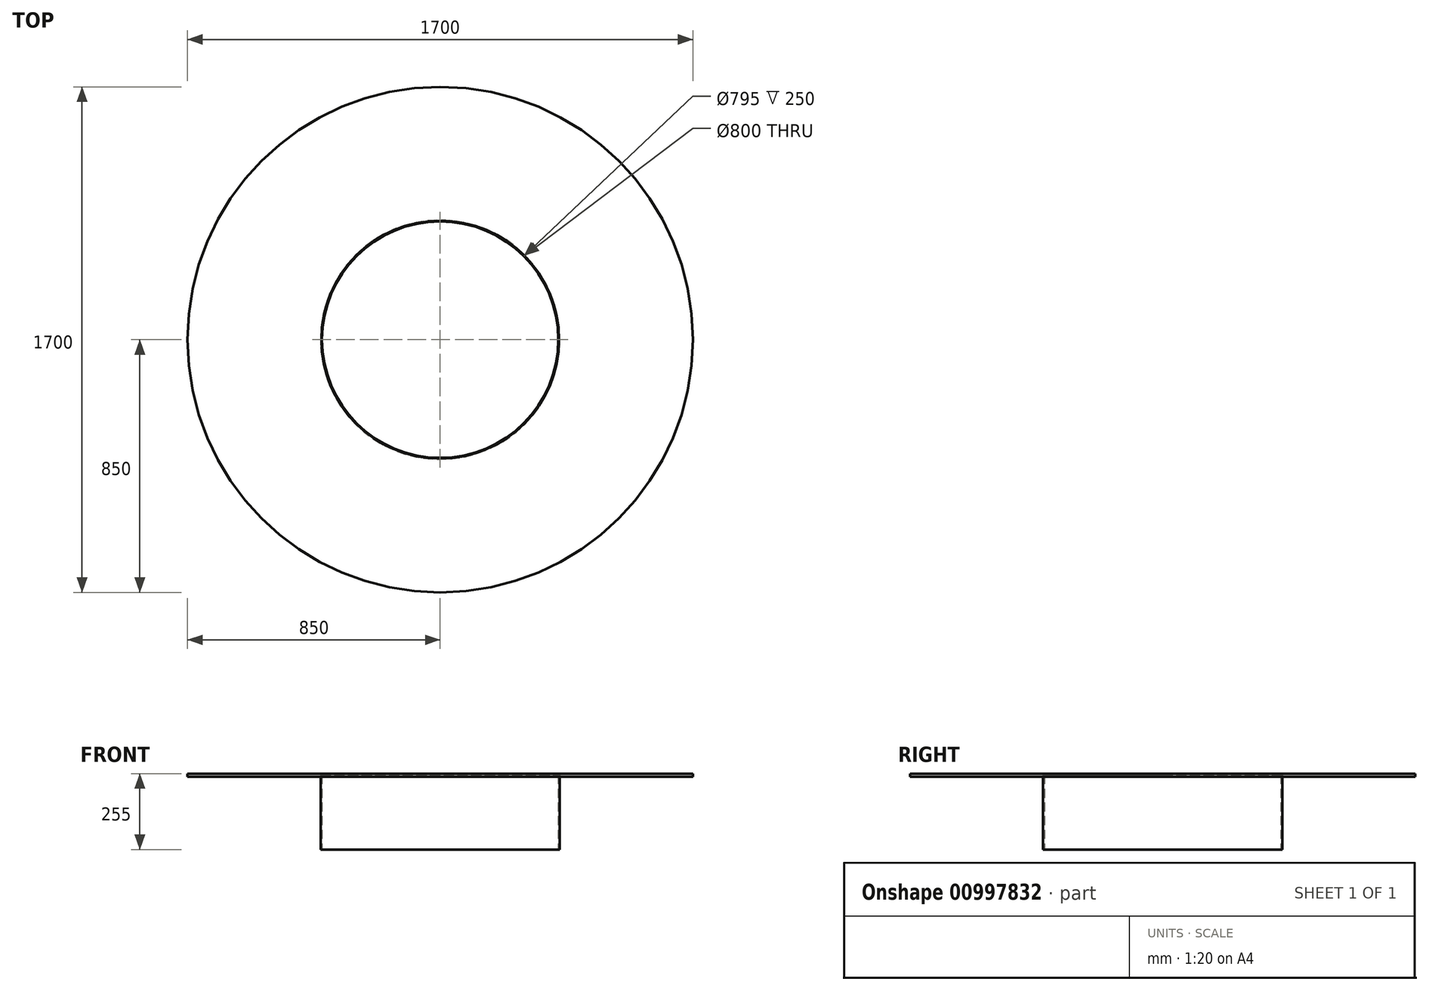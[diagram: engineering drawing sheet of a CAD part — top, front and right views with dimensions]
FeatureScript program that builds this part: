
annotation { "Feature Type Name" : "Feature", "Feature Type Description" : "" }
export const myFeature = defineFeature(function(context is Context, id is Id, definition is map)
    precondition{}
    {
        {
            var Q0;
            Q0=qCreatedBy(makeId("Front.planeOp"),FACE);
            var sketch = newSketch(context, id + "F0", { "sketchPlane" : qUnion([Q0])});
            skLineSegment(sketch, "E0", {"start": v(-1500, 0) * mm, "end": v(1500, 0) * mm, "construction": true});
            skLineSegment(sketch, "E1", {"start": v(-1500, 0) * mm, "end": v(-1561, 697.34) * mm});
            skLineSegment(sketch, "E2", {"start": v(0, 0) * mm, "end": v(0, 1400) * mm, "construction": true});
            skLineSegment(sketch, "E3", {"start": v(-400, 1420) * mm, "end": v(-850, 1420) * mm});
            skLineSegment(sketch, "E4", {"start": v(-850, 1420) * mm, "end": v(-850, 1400) * mm, "construction": true});
            skLineSegment(sketch, "E5", {"start": v(-850, 1400) * mm, "end": v(-400, 1400) * mm});
            skLineSegment(sketch, "E6", {"start": v(-400, 1400) * mm, "end": v(-400, 1420) * mm, "construction": true});
            skLineSegment(sketch, "E7", {"start": v(-860, 1410) * mm, "end": v(-1181.55, 1292.96) * mm});
            skArc(sketch, "E8", {"start": v(-1181.55, 1292.96) * mm, "mid": v(-1472.37, 1059.55) * mm, "end": v(-1561, 697.34) * mm});
            skCircle(sketch, "E9", {"center": v(-400, 1410) * mm, "radius": 10 * mm});
            skCircle(sketch, "E10", {"center": v(-850, 1410) * mm, "radius": 10 * mm});
            skCircle(sketch, "E11", {"center": v(-1500, 0) * mm, "radius": 10 * mm});
            skLineSegment(sketch, "E12", {"start": v(-400, 1410) * mm, "end": v(-400, 1160) * mm, "construction": true});
            skCircle(sketch, "E13", {"center": v(-400, 1160) * mm, "radius": 10 * mm});
            skLineSegment(sketch, "E14", {"start": v(-850, 1410) * mm, "end": v(-400, 1410) * mm, "construction": true});
            skPoint(sketch, "E15", {"position": v(-840, 1410) * mm});
            skPoint(sketch, "E16", {"position": v(-410, 1410) * mm});
            skPoint(sketch, "E17", {"position": v(-400, 1170) * mm});
            skLineSegment(sketch, "E18", {"start": v(-850, 1410) * mm, "end": v(-860, 1410) * mm, "construction": true});
            skPoint(sketch, "E19", {"position": v(-1500.87, 9.96) * mm});
            skSolve(sketch);
        }
        {
            var Q0;
            Q0=sQuery(id+"F0.wireOp",EDGE,"E11");
            var Q1;
            Q1=sQuery(id+"F0.wireOp",EDGE,"E10");
            var Q2;
            Q2=sQuery(id+"F0.wireOp",EDGE,"E9");
            var Q3;
            Q3=sQuery(id+"F0.wireOp",EDGE,"E13");
            var Q4;
            Q4=sQuery(id+"F0.wireOp",EDGE,"E2");
            revolve(context, id + "F1", {"bodyType" : ToolBodyType.SURFACE, "surfaceOperationType" : NewSurfaceOperationType.NEW, "surfaceEntities" : qUnion([Q0, Q1, Q2, Q3]), "axis" : qUnion([Q4]), "revolveType" : RevolveType.FULL});
        }
        {
            var Q0;
            Q0=sQuery(id+"F0.wireOp",EDGE,"E14");
            var Q1;
            Q1=qCreatedBy(makeId("Top.planeOp"),FACE);
            cPlane(context, id + "F2", {"entities" : qUnion([Q0, Q1]), "cplaneType" : CPlaneType.LINE_ANGLE, "offset" : 25 * mm, "angle" : 0 * degree, "width" : 150 * mm, "height" : 150 * mm});
        }
        {
            var Q0;
            Q0=sQuery(id+"F0.wireOp",VERTEX,"E16");
            var Q1;
            Q1=qCreatedBy(makeId("Right.planeOp"),FACE);
            cPlane(context, id + "F3", {"entities" : qUnion([Q0, Q1]), "cplaneType" : CPlaneType.PLANE_POINT, "offset" : 25 * mm, "width" : 150 * mm, "height" : 150 * mm});
        }
        {
            var Q0;
            Q0=qCreatedBy(id+"F3.planeOp",FACE);
            var sketch = newSketch(context, id + "F4", { "sketchPlane" : qUnion([Q0])});
            skCircle(sketch, "E20", {"center": v(0, 1410) * mm, "radius": 10 * mm});
            skSolve(sketch);
        }
        {
            var Q0;
            Q0 = qSketchRegion(id + "F4", true);
            var Q1;
            Q1=makeQuery(id+"F1.opRevolve","SWEPT_FACE",FACE,{"disambiguationData":[OSD([sQuery(id+"F0.wireOp",EDGE,"E10")])]});
            var Q2;
            Q2=sQuery(id+"F0.wireOp",VERTEX,"E15");
            extrude(context, id + "F5", {"entities" : qUnion([Q0]), "endBound" : BoundingType.UP_TO_VERTEX, "oppositeDirection" : true, "depth" : 25 * mm, "endBoundEntityFace" : qUnion([Q1]), "endBoundEntityVertex" : qUnion([Q2]), "offsetDistance" : 25 * mm});
        }
        {
            var Q0;
            Q0=sQuery(id+"F0.wireOp",VERTEX,"E17");
            var Q1;
            Q1=qCreatedBy(makeId("Top.planeOp"),FACE);
            cPlane(context, id + "F6", {"entities" : qUnion([Q0, Q1]), "cplaneType" : CPlaneType.PLANE_POINT, "offset" : 25 * mm, "width" : 150 * mm, "height" : 150 * mm});
        }
        {
            var Q0;
            Q0=qCreatedBy(id+"F6.planeOp",FACE);
            var sketch = newSketch(context, id + "F7", { "sketchPlane" : qUnion([Q0])});
            skCircle(sketch, "E21", {"center": v(-400, 0) * mm, "radius": 10 * mm});
            skSolve(sketch);
        }
        {
            var Q0;
            Q0 = qSketchRegion(id + "F7", true);
            var Q1;
            Q1=sQuery(id+"F0.wireOp",VERTEX,"E5.end");
            extrude(context, id + "F8", {"entities" : qUnion([Q0]), "endBound" : BoundingType.UP_TO_VERTEX, "depth" : 25 * mm, "endBoundEntityVertex" : qUnion([Q1]), "offsetDistance" : 25 * mm});
        }
        {
            var Q0;
            Q0=makeQuery(id+"F8.opExtrude","SWEPT_BODY",BODY,{"disambiguationData":[OSD([sQuery(id+"F7.wireOp",EDGE,"E21")])]});
            var Q1;
            Q1=makeQuery(id+"F5.opExtrude","SWEPT_BODY",BODY,{"disambiguationData":[OSD([sQuery(id+"F4.wireOp",EDGE,"E20")])]});
            var Q2;
            Q2=sQuery(id+"F0.wireOp",EDGE,"E2");
            circularPattern(context, id + "F9", {"entities" : qUnion([Q0, Q1]), "axis" : qUnion([Q2]), "angle" : 360 * degree, "instanceCount" : 16, "equalSpace" : true});
        }
        {
            var Q0;
            Q0=qCreatedBy(makeId("Top.planeOp"),FACE);
            cPlane(context, id + "F10", {"entities" : qUnion([Q0]), "cplaneType" : CPlaneType.OFFSET, "offset" : 10 * mm, "width" : 150 * mm, "height" : 150 * mm});
        }
        {
            var Q0;
            Q0=qCreatedBy(id+"F10.planeOp",FACE);
            var sketch = newSketch(context, id + "F11", { "sketchPlane" : qUnion([Q0])});
            skCircle(sketch, "E22", {"center": v(-1500.87, 0) * mm, "radius": 10 * mm});
            skSolve(sketch);
        }
        {
            var Q0;
            Q0=makeQuery(id+"F11.imprint","IMPRINT",FACE,{"disambiguationData":[TD([[makeQuery(id+"F11.imprint","IMPRINT",EDGE,{"derivedFrom":sQuery(id+"F11.wireOp",EDGE,"E22")}),1.0]])]});
            var Q1;
            Q1=sQuery(id+"F0.wireOp",EDGE,"E1");
            var Q2;
            Q2=sQuery(id+"F0.wireOp",EDGE,"E8");
            var Q3;
            Q3=sQuery(id+"F0.wireOp",EDGE,"E7");
            sweep(context, id + "F12", {"profiles" : qUnion([Q0]), "path" : qUnion([Q1, Q2, Q3])});
        }
        {
            var Q0;
            Q0=makeQuery(id+"F12.opSweep","SWEPT_BODY",BODY,{"disambiguationData":[OSD([sQuery(id+"F0.wireOp",EDGE,"E7"),sQuery(id+"F11.wireOp",EDGE,"E22")])]});
            var Q1;
            Q1=sQuery(id+"F0.wireOp",EDGE,"E2");
            circularPattern(context, id + "F13", {"entities" : qUnion([Q0]), "axis" : qUnion([Q1]), "angle" : 360 * degree, "instanceCount" : 20, "equalSpace" : true});
        }
        {
            var Q0;
            Q0=qCreatedBy(makeId("Front.planeOp"),FACE);
            var sketch = newSketch(context, id + "F14", { "sketchPlane" : qUnion([Q0])});
            skLineSegment(sketch, "E23.bottom", {"start": v(-1630, 1509.63) * mm, "end": v(1696.87, 1509.63) * mm});
            skLineSegment(sketch, "E23.top", {"start": v(-1630, -136) * mm, "end": v(1696.87, -136) * mm});
            skLineSegment(sketch, "E23.left", {"start": v(-1630, 1509.63) * mm, "end": v(-1630, -136) * mm});
            skLineSegment(sketch, "E23.right", {"start": v(1696.87, 1509.63) * mm, "end": v(1696.87, -136) * mm});
            skSolve(sketch);
        }
        {
            var Q0;
            Q0 = qSketchRegion(id + "F14", true);
            extrude(context, id + "F15", {"entities" : qUnion([Q0]), "operationType" : NewBodyOperationType.REMOVE, "endBound" : BoundingType.SYMMETRIC, "oppositeDirection" : true, "depth" : 4000 * mm, "offsetDistance" : 25 * mm});
        }
        {
            var Q0;
            Q0=qCreatedBy(id+"F2.planeOp",FACE);
            var sketch = newSketch(context, id + "F16", { "sketchPlane" : qUnion([Q0])});
            skCircle(sketch, "E24", {"center": v(0, 0) * mm, "radius": 850 * mm});
            skCircle(sketch, "E25", {"center": v(0, 0) * mm, "radius": 400 * mm});
            skSolve(sketch);
        }
        {
            var Q0;
            Q0=makeQuery(id+"F16.imprint","IMPRINT",FACE,{"disambiguationData":[TD([[makeQuery(id+"F16.imprint","IMPRINT",EDGE,{"derivedFrom":sQuery(id+"F16.wireOp",EDGE,"E24")}),1.0]])]});
            extrude(context, id + "F17", {"entities" : qUnion([Q0]), "endBound" : BoundingType.SYMMETRIC, "depth" : 10 * mm, "offsetDistance" : 25 * mm});
        }
        {
            var Q0;
            Q0=qCreatedBy(makeId("Front.planeOp"),FACE);
            var sketch = newSketch(context, id + "F18", { "sketchPlane" : qUnion([Q0])});
            skLineSegment(sketch, "E26.0", {"start": v(-402.5, 1410) * mm, "end": v(-402.5, 1160) * mm});
            skLineSegment(sketch, "E27.0", {"start": v(-397.5, 1410) * mm, "end": v(-397.5, 1160) * mm});
            skLineSegment(sketch, "E28", {"start": v(-402.5, 1160) * mm, "end": v(-397.5, 1160) * mm});
            skLineSegment(sketch, "E29", {"start": v(-402.5, 1410) * mm, "end": v(-397.5, 1410) * mm});
            skSolve(sketch);
        }
        {
            var Q0;
            Q0 = qSketchRegion(id + "F18", true);
            var Q1;
            Q1=sQuery(id+"F0.wireOp",EDGE,"E2");
            revolve(context, id + "F19", {"surfaceOperationType" : NewSurfaceOperationType.NEW, "entities" : qUnion([Q0]), "axis" : qUnion([Q1]), "revolveType" : RevolveType.FULL});
        }
    });
